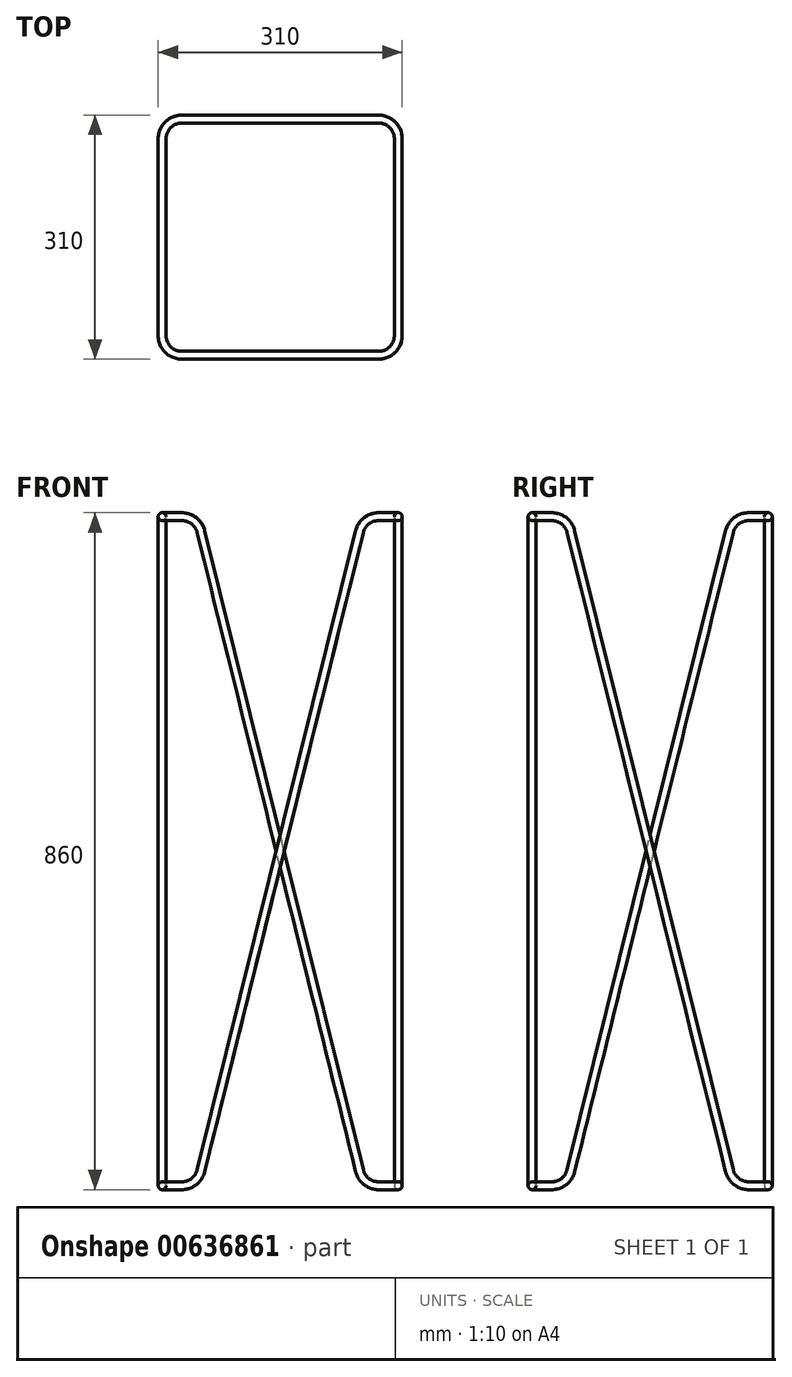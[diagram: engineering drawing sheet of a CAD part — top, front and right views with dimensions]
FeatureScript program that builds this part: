
annotation { "Feature Type Name" : "Feature", "Feature Type Description" : "" }
export const myFeature = defineFeature(function(context is Context, id is Id, definition is map)
    precondition{}
    {
        {
            var Q0;
            Q0=qCreatedBy(makeId("Top.planeOp"),FACE);
            var sketch = newSketch(context, id + "F0", { "sketchPlane" : qUnion([Q0])});
            skLineSegment(sketch, "E0.bottom", {"start": v(-150, -150) * mm, "end": v(150, -150) * mm, "construction": true});
            skLineSegment(sketch, "E0.top", {"start": v(-150, 150) * mm, "end": v(150, 150) * mm, "construction": true});
            skLineSegment(sketch, "E0.left", {"start": v(-150, -150) * mm, "end": v(-150, 150) * mm, "construction": true});
            skLineSegment(sketch, "E0.right", {"start": v(150, -150) * mm, "end": v(150, 150) * mm, "construction": true});
            skPoint(sketch, "E0.middle", {"position": v(0, 0) * mm});
            skArc(sketch, "E1", {"start": v(-150, -125) * mm, "mid": v(-142.68, -142.68) * mm, "end": v(-125, -150) * mm});
            skArc(sketch, "E2", {"start": v(150, 125) * mm, "mid": v(142.68, 142.68) * mm, "end": v(125, 150) * mm});
            skArc(sketch, "E3", {"start": v(-125, 150) * mm, "mid": v(-142.68, 142.68) * mm, "end": v(-150, 125) * mm});
            skArc(sketch, "E4", {"start": v(125, -150) * mm, "mid": v(142.68, -142.68) * mm, "end": v(150, -125) * mm});
            skSolve(sketch);
        }
        {
            var Q0;
            Q0=qCreatedBy(makeId("Front.planeOp"),FACE);
            cPlane(context, id + "F1", {"entities" : qUnion([Q0]), "cplaneType" : CPlaneType.OFFSET, "offset" : 150 * mm, "width" : 150 * mm, "height" : 150 * mm});
        }
        {
            var Q0;
            Q0=qCreatedBy(id+"F1.planeOp",FACE);
            var sketch = newSketch(context, id + "F2", { "sketchPlane" : qUnion([Q0])});
            skLineSegment(sketch, "E5", {"start": v(-150, 0) * mm, "end": v(-150, -850) * mm, "construction": true});
            skLineSegment(sketch, "E6", {"start": v(150, -850) * mm, "end": v(150, 0) * mm, "construction": true});
            skLineSegment(sketch, "E7", {"start": v(-150, -850) * mm, "end": v(150, -850) * mm, "construction": true});
            skLineSegment(sketch, "E8", {"start": v(-150, 0) * mm, "end": v(150, 0) * mm, "construction": true});
            skArc(sketch, "E9", {"start": v(-100.74, -18.98) * mm, "mid": v(-109.6, -5.3) * mm, "end": v(-125, 0) * mm});
            skLineSegment(sketch, "E10", {"start": v(-100.74, -18.98) * mm, "end": v(100.74, -831.02) * mm});
            skArc(sketch, "E11", {"start": v(100.74, -831.02) * mm, "mid": v(109.6, -844.7) * mm, "end": v(125, -850) * mm});
            skSolve(sketch);
        }
        {
            var Q0;
            Q0=qCreatedBy(makeId("Right.planeOp"),FACE);
            cPlane(context, id + "F3", {"entities" : qUnion([Q0]), "cplaneType" : CPlaneType.OFFSET, "offset" : 150 * mm, "width" : 150 * mm, "height" : 150 * mm});
        }
        {
            var Q0;
            Q0=qCreatedBy(makeId("Right.planeOp"),FACE);
            cPlane(context, id + "F4", {"entities" : qUnion([Q0]), "cplaneType" : CPlaneType.OFFSET, "offset" : 150 * mm, "oppositeDirection" : true, "width" : 150 * mm, "height" : 150 * mm});
        }
        {
            var Q0;
            Q0=qCreatedBy(id+"F4.planeOp",FACE);
            var sketch = newSketch(context, id + "F5", { "sketchPlane" : qUnion([Q0])});
            skArc(sketch, "E12", {"start": v(-100.74, -18.98) * mm, "mid": v(-109.6, -5.3) * mm, "end": v(-125, 0) * mm});
            skLineSegment(sketch, "E13", {"start": v(-100.74, -18.98) * mm, "end": v(100.74, -831.02) * mm});
            skArc(sketch, "E14", {"start": v(100.74, -831.02) * mm, "mid": v(109.6, -844.7) * mm, "end": v(125, -850) * mm});
            skLineSegment(sketch, "E15", {"start": v(150, 0) * mm, "end": v(150, -850) * mm, "construction": true});
            skLineSegment(sketch, "E16", {"start": v(150, -850) * mm, "end": v(-150, -850) * mm, "construction": true});
            skLineSegment(sketch, "E17", {"start": v(-150, -850) * mm, "end": v(-150, 0) * mm, "construction": true});
            skLineSegment(sketch, "E18", {"start": v(-150, 0) * mm, "end": v(150, 0) * mm, "construction": true});
            skSolve(sketch);
        }
        {
            var Q0;
            Q0=qCreatedBy(makeId("Top.planeOp"),FACE);
            cPlane(context, id + "F6", {"entities" : qUnion([Q0]), "cplaneType" : CPlaneType.OFFSET, "offset" : 850 * mm, "oppositeDirection" : true, "width" : 150 * mm, "height" : 150 * mm});
        }
        {
            var Q0;
            Q0=qCreatedBy(id+"F6.planeOp",FACE);
            var sketch = newSketch(context, id + "F7", { "sketchPlane" : qUnion([Q0])});
            skLineSegment(sketch, "E19.bottom", {"start": v(150, -150) * mm, "end": v(-150, -150) * mm, "construction": true});
            skLineSegment(sketch, "E19.top", {"start": v(150, 150) * mm, "end": v(-150, 150) * mm, "construction": true});
            skLineSegment(sketch, "E19.left", {"start": v(150, -150) * mm, "end": v(150, 150) * mm, "construction": true});
            skLineSegment(sketch, "E19.right", {"start": v(-150, -150) * mm, "end": v(-150, 150) * mm, "construction": true});
            skPoint(sketch, "E19.middle", {"position": v(0, 0) * mm});
            skArc(sketch, "E20.0", {"start": v(-150, -125) * mm, "mid": v(-142.68, -142.68) * mm, "end": v(-125, -150) * mm});
            skArc(sketch, "E20.1", {"start": v(125, -150) * mm, "mid": v(142.68, -142.68) * mm, "end": v(150, -125) * mm});
            skArc(sketch, "E20.2", {"start": v(-125, 150) * mm, "mid": v(-142.68, 142.68) * mm, "end": v(-150, 125) * mm});
            skArc(sketch, "E20.3", {"start": v(150, 125) * mm, "mid": v(142.68, 142.68) * mm, "end": v(125, 150) * mm});
            skSolve(sketch);
        }
        {
            var Q0;
            Q0=qCreatedBy(makeId("Front.planeOp"),FACE);
            var Q1;
            Q1=sQuery(id+"F0.wireOp",VERTEX,"E4.end");
            cPlane(context, id + "F8", {"entities" : qUnion([Q0, Q1]), "cplaneType" : CPlaneType.PLANE_POINT, "offset" : 25 * mm, "width" : 150 * mm, "height" : 150 * mm});
        }
        {
            var Q0;
            Q0=qCreatedBy(id+"F8.planeOp",FACE);
            var sketch = newSketch(context, id + "F9", { "sketchPlane" : qUnion([Q0])});
            skCircle(sketch, "E21", {"center": v(150, -850) * mm, "radius": 5 * mm});
            skSolve(sketch);
        }
        {
            var Q0;
            Q0=makeQuery(id+"F9.imprint","IMPRINT",FACE,{"disambiguationData":[TD([[makeQuery(id+"F9.imprint","IMPRINT",EDGE,{"derivedFrom":sQuery(id+"F9.wireOp",EDGE,"E21")}),1.0]])]});
            var Q1;
            Q1=sQuery(id+"F7.wireOp",EDGE,"E20.1");
            var Q2;
            Q2=sQuery(id+"F2.wireOp",EDGE,"E11");
            var Q3;
            Q3=sQuery(id+"F2.wireOp",EDGE,"E10");
            var Q4;
            Q4=sQuery(id+"F2.wireOp",EDGE,"E9");
            var Q5;
            Q5=sQuery(id+"F0.wireOp",EDGE,"E1");
            var Q6;
            Q6=sQuery(id+"F5.wireOp",EDGE,"E12");
            var Q7;
            Q7=sQuery(id+"F5.wireOp",EDGE,"E13");
            var Q8;
            Q8=sQuery(id+"F5.wireOp",EDGE,"E14");
            var Q9;
            Q9=sQuery(id+"F7.wireOp",EDGE,"E20.2");
            sweep(context, id + "F10", {"profiles" : qUnion([Q0]), "path" : qUnion([Q1, Q2, Q3, Q4, Q5, Q6, Q7, Q8, Q9])});
        }
        {
            var Q0;
            Q0=qCreatedBy(id+"F6.planeOp",FACE);
            var sketch = newSketch(context, id + "F11", { "sketchPlane" : qUnion([Q0])});
            skLineSegment(sketch, "E22", {"start": v(150, -150) * mm, "end": v(-229, 229) * mm, "construction": true});
            skSolve(sketch);
        }
        {
            var Q0;
            Q0=sQuery(id+"F11.wireOp",EDGE,"E22");
            var Q1;
            Q1=qCreatedBy(makeId("Right.planeOp"),FACE);
            cPlane(context, id + "F12", {"entities" : qUnion([Q0, Q1]), "cplaneType" : CPlaneType.LINE_ANGLE, "offset" : 25 * mm, "angle" : 0 * degree, "width" : 150 * mm, "height" : 150 * mm});
        }
        {
            var Q0;
            Q0=makeQuery(id+"F10.opSweep","SWEPT_BODY",BODY,{"disambiguationData":[OSD([sQuery(id+"F7.wireOp",EDGE,"E20.2"),sQuery(id+"F9.wireOp",EDGE,"E21")])]});
            var Q1;
            Q1=qCreatedBy(id+"F12.planeOp",FACE);
            mirror(context, id + "F13", {"operationType" : NewBodyOperationType.ADD, "entities" : qUnion([Q0]), "mirrorPlane" : qUnion([Q1])});
        }
        {
            var Q0;
            Q0=qCreatedBy(makeId("Front.planeOp"),FACE);
            var sketch = newSketch(context, id + "F14", { "sketchPlane" : qUnion([Q0])});
            skLineSegment(sketch, "E23", {"start": v(0, 0) * mm, "end": v(0, -1427.26) * mm, "construction": true});
            skSolve(sketch);
        }
        {
            var Q0;
            Q0=makeQuery(id+"F10.opSweep","SWEPT_BODY",BODY,{"disambiguationData":[OSD([sQuery(id+"F7.wireOp",EDGE,"E20.2"),sQuery(id+"F9.wireOp",EDGE,"E21")])]});
            var Q1;
            Q1=sQuery(id+"F14.wireOp",EDGE,"E23");
            circularPattern(context, id + "F15", {"entities" : qUnion([Q0]), "axis" : qUnion([Q1]), "angle" : 360 * degree, "instanceCount" : 4, "equalSpace" : true});
        }
        {
            var Q0;
            Q0=qCreatedBy(makeId("Top.planeOp"),FACE);
            cPlane(context, id + "F16", {"entities" : qUnion([Q0]), "cplaneType" : CPlaneType.OFFSET, "offset" : 3 * mm, "width" : 150 * mm, "height" : 150 * mm});
        }
        {
            var Q0;
            Q0=makeQuery(id+"F15.opPattern","COPY",BODY,{"derivedFrom":makeQuery(id+"F10.opSweep","SWEPT_BODY",BODY,{"disambiguationData":[OSD([sQuery(id+"F7.wireOp",EDGE,"E20.2"),sQuery(id+"F9.wireOp",EDGE,"E21")])]}),"instanceName":"2"});
            deleteBodies(context, id + "F17", {"entities" : qUnion([Q0])});
        }
        {
            var Q0;
            Q0=makeQuery(id+"F15.opPattern","COPY",BODY,{"derivedFrom":makeQuery(id+"F10.opSweep","SWEPT_BODY",BODY,{"disambiguationData":[OSD([sQuery(id+"F7.wireOp",EDGE,"E20.2"),sQuery(id+"F9.wireOp",EDGE,"E21")])]}),"instanceName":"3"});
            deleteBodies(context, id + "F18", {"entities" : qUnion([Q0])});
        }
    });
